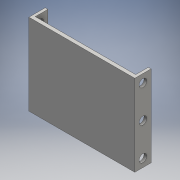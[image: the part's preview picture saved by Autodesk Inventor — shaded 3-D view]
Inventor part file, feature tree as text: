
AUTODESK INVENTOR PART (.ipt)
format: ipt  version: 2016 (Build 200138000, 138)  size: 119,808 bytes
history: native  units: mm
features: sketch x3, extrude x2, hole x1
ambient origin geometry x8: Origin, YZ Plane, XZ Plane, XY Plane, X Axis, Y Axis, Z Axis, Center Point
bodies: Solid1 (feature_tree)
feature tree (6):
  extrude  "Extrusion1"  Depth=45.0mm
  extrude  "Extrusion2"  Depth=1.5mm
  hole  "Hole1"  [1 undecoded]
  sketch  "Sketch1"  dims[d0=55.5mm d1=45.0mm]
  sketch  "Sketch2"  dims[d2=2.0mm d3=0.0mm d4=1.5mm]
  sketch  "Sketch3"  dims[d5=1.5mm d6=9.0mm d7=0.0mm d8=4.3mm d9=4.5mm d10=4.5mm d11=4.3mm d12=4.5mm d13=4.5mm d14=4.3mm d15=4.3mm d16=6.0mm d17=4.0mm d18=2.0mm d19=90.0deg d20=8.0mm d21=20.594885mm]
note: 1 required parameter value undecoded (feature->parameter linkage not recoverable at this tier; creation-order binding heuristic only, values carry confidence <= 0.55)
